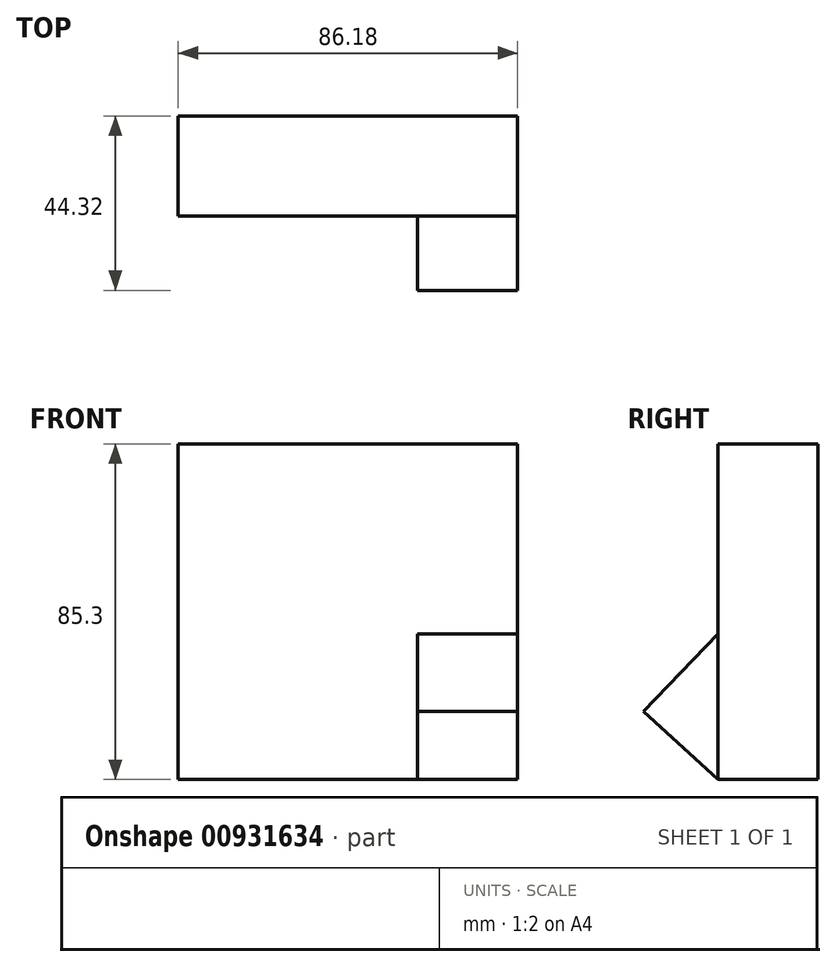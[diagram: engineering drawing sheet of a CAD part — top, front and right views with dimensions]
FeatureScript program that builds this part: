
annotation { "Feature Type Name" : "Feature", "Feature Type Description" : "" }
export const myFeature = defineFeature(function(context is Context, id is Id, definition is map)
    precondition{}
    {
        {
            var Q0;
            Q0=qCreatedBy(makeId("Front.planeOp"),FACE);
            var sketch = newSketch(context, id + "F0", { "sketchPlane" : qUnion([Q0])});
            skLineSegment(sketch, "E0.bottom", {"start": v(-45.3, 44.5) * mm, "end": v(40.89, 44.5) * mm});
            skLineSegment(sketch, "E0.top", {"start": v(-45.3, -40.8) * mm, "end": v(40.89, -40.8) * mm});
            skLineSegment(sketch, "E0.left", {"start": v(-45.3, 44.5) * mm, "end": v(-45.3, -40.8) * mm});
            skLineSegment(sketch, "E0.right", {"start": v(40.89, 44.5) * mm, "end": v(40.89, -40.8) * mm});
            skSolve(sketch);
        }
        {
            var Q0;
            Q0=makeQuery(id+"F0.imprint","IMPRINT",FACE,{"disambiguationData":[TD([[makeQuery(id+"F0.imprint","IMPRINT",EDGE,{"derivedFrom":sQuery(id+"F0.wireOp",EDGE,"E0.bottom")}),-1.0]])]});
            extrude(context, id + "F1", {"entities" : qUnion([Q0]), "depth" : 25.4 * mm, "offsetDistance" : 25.4 * mm});
        }
        {
            var Q0;
            Q0=makeQuery(id+"F1.opExtrude","SWEPT_FACE",FACE,{"disambiguationData":[OSD([sQuery(id+"F0.wireOp",EDGE,"E0.right")])]});
            var sketch = newSketch(context, id + "F2", { "sketchPlane" : qUnion([Q0])});
            skLineSegment(sketch, "E1", {"start": v(-25.4, -3.79) * mm, "end": v(-44.32, -23.53) * mm});
            skLineSegment(sketch, "E2", {"start": v(-44.32, -23.53) * mm, "end": v(-25.4, -40.8) * mm});
            skSolve(sketch);
        }
        {
            var Q0;
            {var subQ0=sQuery(id+"F2.wireOp",EDGE,"E1");Q0=makeQuery(id+"F2.imprint","IMPRINT",FACE,{"disambiguationData":[TD([[makeQuery(id+"F2.imprint","IMPRINT",EDGE,{"derivedFrom":subQ0}),1.0]])]});}
            extrude(context, id + "F3", {"entities" : qUnion([Q0]), "oppositeDirection" : true, "depth" : 25.4 * mm, "offsetDistance" : 25.4 * mm});
        }
    });
